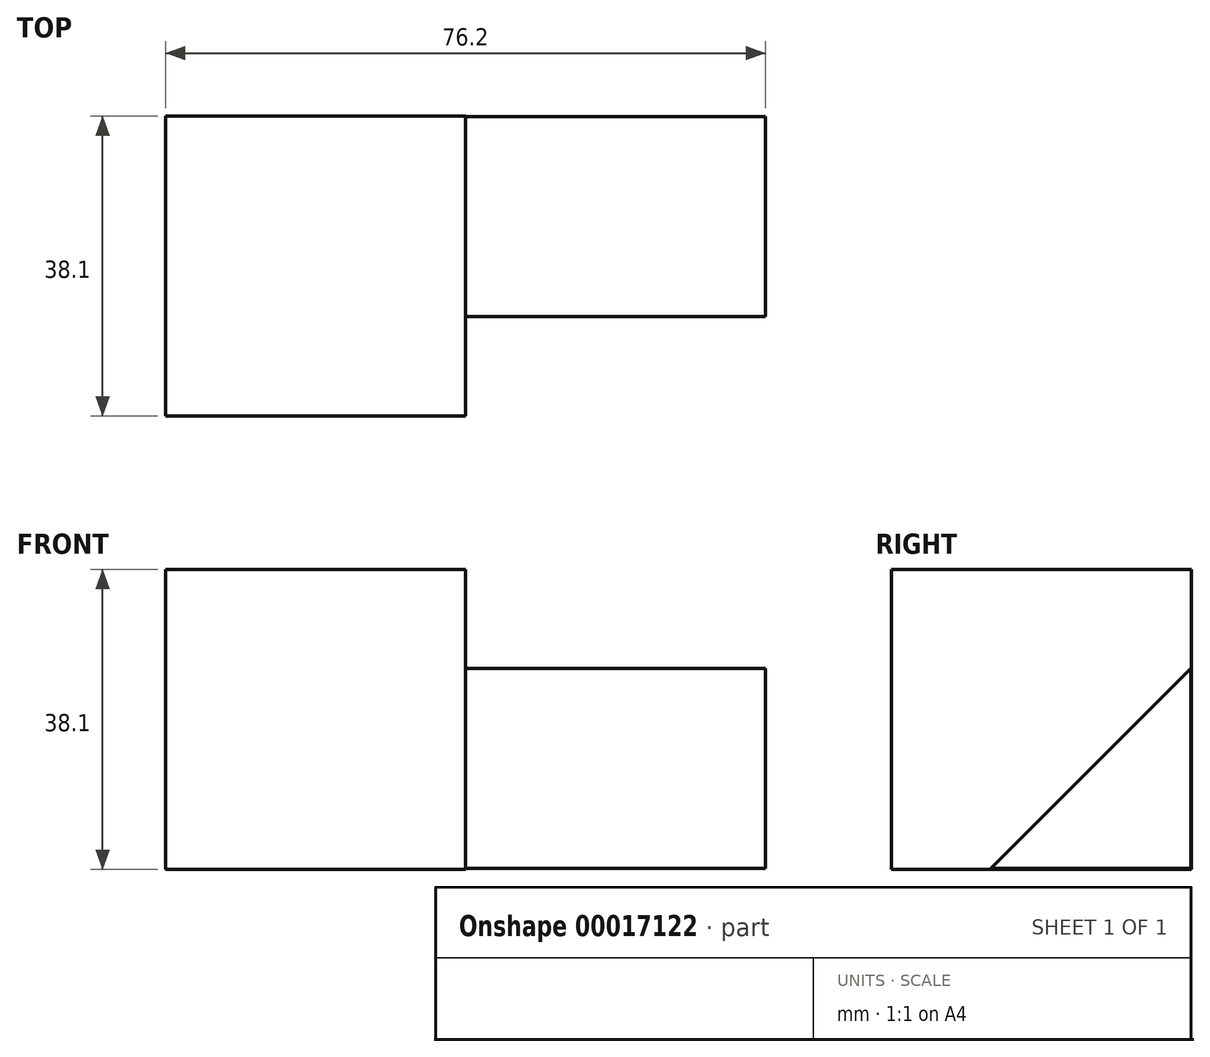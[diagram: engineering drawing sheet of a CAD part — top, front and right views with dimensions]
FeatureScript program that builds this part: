
annotation { "Feature Type Name" : "Feature", "Feature Type Description" : "" }
export const myFeature = defineFeature(function(context is Context, id is Id, definition is map)
    precondition{}
    {
        {
            var Q0;
            Q0=qCreatedBy(makeId("Right.planeOp"),FACE);
            var sketch = newSketch(context, id + "F0", { "sketchPlane" : qUnion([Q0])});
            skLineSegment(sketch, "E0.bottom", {"start": v(-30.35, 21.33) * mm, "end": v(7.75, 21.33) * mm});
            skLineSegment(sketch, "E0.top", {"start": v(-30.35, -16.77) * mm, "end": v(7.75, -16.77) * mm});
            skLineSegment(sketch, "E0.left", {"start": v(-30.35, 21.33) * mm, "end": v(-30.35, -16.77) * mm});
            skLineSegment(sketch, "E0.right", {"start": v(7.75, 21.33) * mm, "end": v(7.75, -16.77) * mm});
            skSolve(sketch);
        }
        {
            var Q0;
            Q0=qCreatedBy(makeId("Right.planeOp"),FACE);
            var sketch = newSketch(context, id + "F1", { "sketchPlane" : qUnion([Q0])});
            skLineSegment(sketch, "E1", {"start": v(7.67, -16.65) * mm, "end": v(7.67, 8.75) * mm});
            skLineSegment(sketch, "E2", {"start": v(7.67, 8.75) * mm, "end": v(-17.73, -16.65) * mm});
            skLineSegment(sketch, "E3", {"start": v(-17.73, -16.65) * mm, "end": v(7.67, -16.65) * mm});
            skSolve(sketch);
        }
        {
            var Q0;
            Q0 = qSketchRegion(id + "F1", true);
            extrude(context, id + "F2", {"entities" : qUnion([Q0]), "depth" : 38.1 * mm});
        }
        {
            var Q0;
            Q0=makeQuery(id+"F0.imprint","IMPRINT",FACE,{"disambiguationData":[TD([[makeQuery(id+"F0.imprint","IMPRINT",EDGE,{"derivedFrom":sQuery(id+"F0.wireOp",EDGE,"E0.bottom")}),-1.0]])]});
            extrude(context, id + "F3", {"entities" : qUnion([Q0]), "operationType" : NewBodyOperationType.ADD, "oppositeDirection" : true, "depth" : 38.1 * mm});
        }
    });
